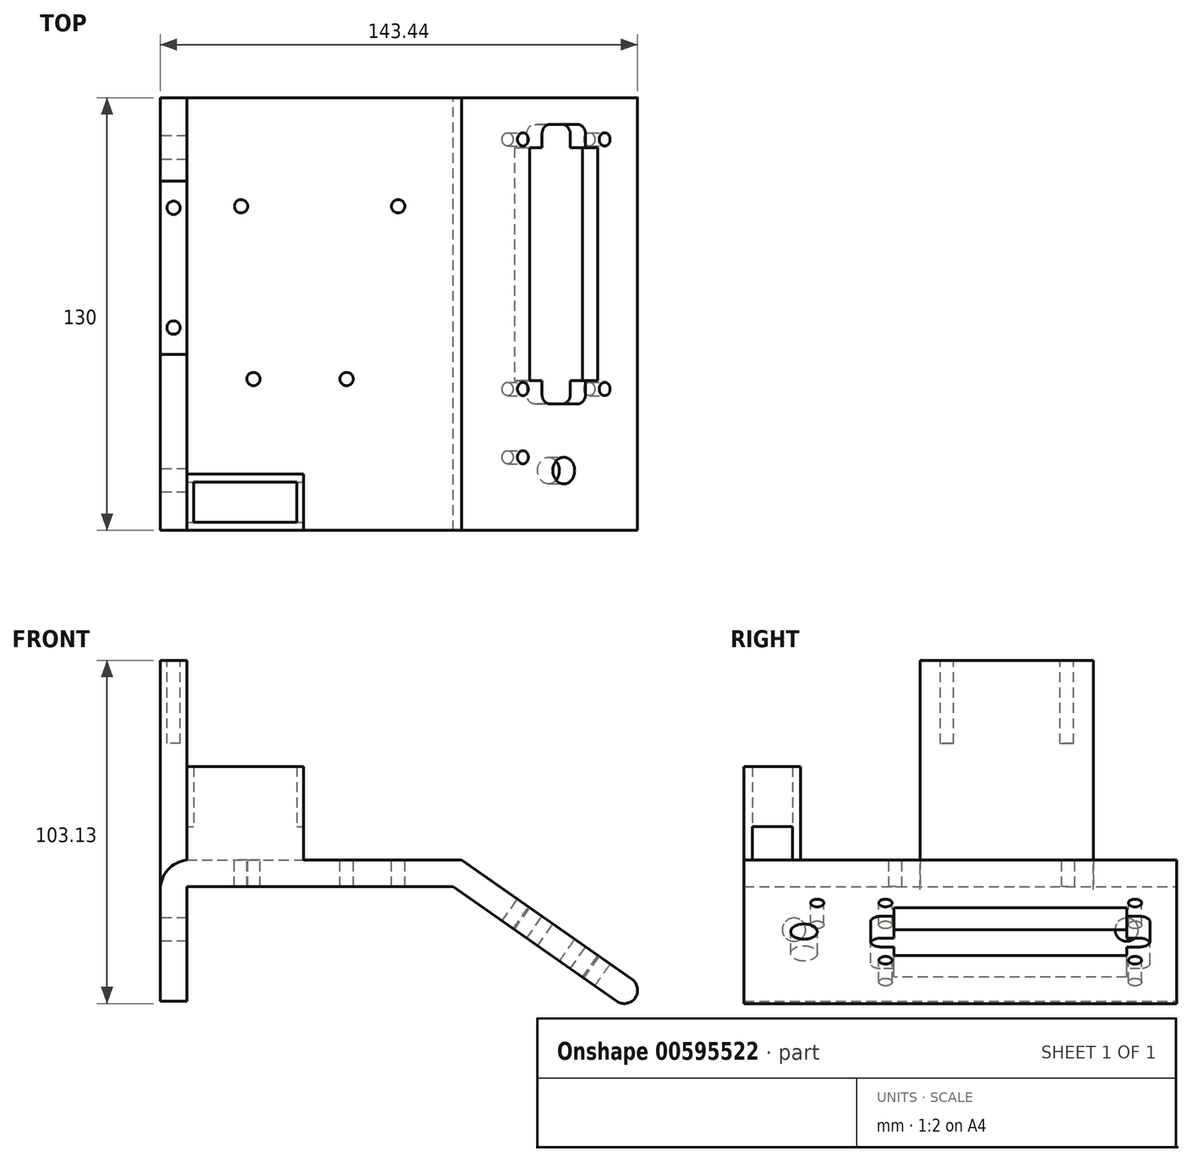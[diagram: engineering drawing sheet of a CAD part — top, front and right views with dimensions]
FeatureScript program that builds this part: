
annotation { "Feature Type Name" : "Feature", "Feature Type Description" : "" }
export const myFeature = defineFeature(function(context is Context, id is Id, definition is map)
    precondition{}
    {
        {
            var Q0;
            Q0=qCreatedBy(makeId("Front.planeOp"),FACE);
            var sketch = newSketch(context, id + "F0", { "sketchPlane" : qUnion([Q0])});
            skLineSegment(sketch, "E0", {"start": v(89.15, 0) * mm, "end": v(40, 34.41) * mm});
            skLineSegment(sketch, "E1", {"start": v(40, 34.41) * mm, "end": v(-40, 34.41) * mm});
            skLineSegment(sketch, "E2", {"start": v(-37.03, 0) * mm, "end": v(89.15, 0) * mm, "construction": true});
            skLineSegment(sketch, "E3", {"start": v(0, 34.41) * mm, "end": v(0, 0) * mm, "construction": true});
            skLineSegment(sketch, "E4.0", {"start": v(42.52, 42.41) * mm, "end": v(-40, 42.41) * mm});
            skLineSegment(sketch, "E4.1", {"start": v(93.74, 6.55) * mm, "end": v(42.52, 42.41) * mm});
            skLineSegment(sketch, "E5", {"start": v(-40, 42.41) * mm, "end": v(-40, 34.41) * mm, "construction": true});
            skLineSegment(sketch, "E6", {"start": v(93.74, 6.55) * mm, "end": v(89.15, 0) * mm, "construction": true});
            skArc(sketch, "E7", {"start": v(89.15, 0) * mm, "mid": v(94.72, 0.98) * mm, "end": v(93.74, 6.55) * mm});
            skLineSegment(sketch, "E8", {"start": v(-40, 34.41) * mm, "end": v(-40, 0) * mm});
            skLineSegment(sketch, "E9.0", {"start": v(-48, 33.47) * mm, "end": v(-48, 0) * mm});
            skArc(sketch, "E10", {"start": v(-40, 42.41) * mm, "mid": v(-45.7, 39.47) * mm, "end": v(-48, 33.47) * mm});
            skLineSegment(sketch, "E11", {"start": v(-40, 0) * mm, "end": v(-48, 0) * mm});
            skSolve(sketch);
        }
        {
            var Q0;
            Q0=makeQuery(id+"F0.imprint","IMPRINT",FACE,{"disambiguationData":[TD([[makeQuery(id+"F0.imprint","IMPRINT",EDGE,{"derivedFrom":sQuery(id+"F0.wireOp",EDGE,"E0")}),-1.0]])]});
            extrude(context, id + "F1", {"entities" : qUnion([Q0]), "depth" : 80 * mm, "offsetDistance" : 25 * mm, "hasSecondDirection" : true, "secondDirectionOppositeDirection" : true, "secondDirectionDepth" : 50 * mm});
        }
        {
            var Q0;
            Q0=makeQuery(id+"F1.opExtrude","SWEPT_FACE",FACE,{"disambiguationData":[OSD([sQuery(id+"F0.wireOp",EDGE,"E4.1")])]});
            var sketch = newSketch(context, id + "F2", { "sketchPlane" : qUnion([Q0])});
            skLineSegment(sketch, "E12.bottom", {"start": v(35.53, -35) * mm, "end": v(40.03, -35) * mm});
            skLineSegment(sketch, "E12.top", {"start": v(35.53, 35) * mm, "end": v(60.53, 35) * mm});
            skLineSegment(sketch, "E12.left", {"start": v(35.53, -35) * mm, "end": v(35.53, 35) * mm});
            skLineSegment(sketch, "E12.right", {"start": v(60.53, -35) * mm, "end": v(60.53, 35) * mm});
            skPoint(sketch, "E12.middle", {"position": v(48.03, 0) * mm});
            skLineSegment(sketch, "E13.bottom", {"start": v(63.03, 37.5) * mm, "end": v(33.03, 37.5) * mm, "construction": true});
            skLineSegment(sketch, "E13.top", {"start": v(63.03, -37.5) * mm, "end": v(33.03, -37.5) * mm, "construction": true});
            skLineSegment(sketch, "E13.left", {"start": v(63.03, 37.5) * mm, "end": v(63.03, -37.5) * mm, "construction": true});
            skLineSegment(sketch, "E13.right", {"start": v(33.03, 37.5) * mm, "end": v(33.03, -37.5) * mm, "construction": true});
            skCircle(sketch, "E14", {"center": v(33.03, -37.5) * mm, "radius": 2 * mm});
            skCircle(sketch, "E15", {"center": v(33.03, 37.5) * mm, "radius": 2 * mm});
            skCircle(sketch, "E16", {"center": v(63.03, 37.5) * mm, "radius": 2 * mm});
            skCircle(sketch, "E17", {"center": v(63.03, -37.5) * mm, "radius": 2 * mm});
            skLineSegment(sketch, "E18.bottom", {"start": v(43.03, -42) * mm, "end": v(53.03, -42) * mm});
            skLineSegment(sketch, "E18.top", {"start": v(40.03, -28) * mm, "end": v(56.03, -28) * mm, "construction": true});
            skLineSegment(sketch, "E18.left", {"start": v(40.03, -39) * mm, "end": v(40.03, -35) * mm});
            skLineSegment(sketch, "E18.right", {"start": v(56.03, -39) * mm, "end": v(56.03, -35) * mm});
            skPoint(sketch, "E18.middle", {"position": v(48.03, -35) * mm});
            skLineSegment(sketch, "E19", {"start": v(40.03, -35) * mm, "end": v(40.03, -28) * mm, "construction": true});
            skLineSegment(sketch, "E20", {"start": v(56.03, -35) * mm, "end": v(56.03, -28) * mm, "construction": true});
            skLineSegment(sketch, "E21", {"start": v(56.03, -35) * mm, "end": v(60.53, -35) * mm});
            skLineSegment(sketch, "E22", {"start": v(40.03, -35) * mm, "end": v(56.03, -35) * mm, "construction": true});
            skLineSegment(sketch, "E23", {"start": v(10.5, -15) * mm, "end": v(73.03, -15) * mm, "construction": true});
            skPoint(sketch, "E24.visualSharp", {"position": v(40.03, -42) * mm});
            skArc(sketch, "E24.filletArc", {"start": v(40.03, -39) * mm, "mid": v(40.9, -41.12) * mm, "end": v(43.03, -42) * mm});
            skPoint(sketch, "E25.visualSharp", {"position": v(56.03, -42) * mm});
            skArc(sketch, "E25.filletArc", {"start": v(53.03, -42) * mm, "mid": v(55.15, -41.12) * mm, "end": v(56.03, -39) * mm});
            skLineSegment(sketch, "E26.bottom", {"start": v(40.03, 28) * mm, "end": v(56.03, 28) * mm, "construction": true});
            skLineSegment(sketch, "E26.top", {"start": v(43.03, 42) * mm, "end": v(53.03, 42) * mm});
            skLineSegment(sketch, "E26.left", {"start": v(40.03, 28) * mm, "end": v(40.03, 35) * mm, "construction": true});
            skLineSegment(sketch, "E26.right", {"start": v(56.03, 28) * mm, "end": v(56.03, 35) * mm, "construction": true});
            skPoint(sketch, "E26.middle", {"position": v(48.03, 35) * mm});
            skLineSegment(sketch, "E27", {"start": v(40.03, 35) * mm, "end": v(40.03, 35.04) * mm});
            skLineSegment(sketch, "E28", {"start": v(56.03, 35) * mm, "end": v(56.03, 35) * mm});
            skLineSegment(sketch, "E29", {"start": v(40.03, 35.04) * mm, "end": v(40.03, 39) * mm});
            skLineSegment(sketch, "E30", {"start": v(56.03, 35) * mm, "end": v(56.03, 39) * mm});
            skPoint(sketch, "E31.visualSharp", {"position": v(40.03, 42) * mm});
            skArc(sketch, "E31.filletArc", {"start": v(43.03, 42) * mm, "mid": v(40.9, 41.12) * mm, "end": v(40.03, 39) * mm});
            skPoint(sketch, "E32.visualSharp", {"position": v(56.03, 42) * mm});
            skArc(sketch, "E32.filletArc", {"start": v(56.03, 39) * mm, "mid": v(55.15, 41.12) * mm, "end": v(53.03, 42) * mm});
            skSolve(sketch);
        }
        {
            var Q0;
            Q0 = qSketchRegion(id + "F2", true);
            extrude(context, id + "F3", {"entities" : qUnion([Q0]), "operationType" : NewBodyOperationType.REMOVE, "oppositeDirection" : true, "depth" : 25 * mm, "offsetDistance" : 25 * mm});
        }
        {
            var Q0;
            Q0=makeQuery(id+"F1.opExtrude","SWEPT_FACE",FACE,{"disambiguationData":[OSD([sQuery(id+"F0.wireOp",EDGE,"E4.0")])]});
            var sketch = newSketch(context, id + "F4", { "sketchPlane" : qUnion([Q0])});
            skLineSegment(sketch, "E33.bottom", {"start": v(27, 33) * mm, "end": v(-27, 33) * mm, "construction": true});
            skLineSegment(sketch, "E33.top", {"start": v(27, -37) * mm, "end": v(-27, -37) * mm, "construction": true});
            skLineSegment(sketch, "E33.left", {"start": v(27, 33) * mm, "end": v(27, -37) * mm, "construction": true});
            skLineSegment(sketch, "E33.right", {"start": v(-27, 33) * mm, "end": v(-27, -37) * mm, "construction": true});
            skPoint(sketch, "E33.middle", {"position": v(0, -2) * mm});
            skLineSegment(sketch, "E34", {"start": v(40, 13) * mm, "end": v(-42.52, 13) * mm, "construction": true});
            skLineSegment(sketch, "E35", {"start": v(0, 78) * mm, "end": v(0, -52) * mm, "construction": true});
            skPoint(sketch, "E35.startSnap0", {"position": v(-1.26, 78) * mm});
            skCircle(sketch, "E36", {"center": v(8, -34.5) * mm, "radius": 2 * mm});
            skCircle(sketch, "E37", {"center": v(-20, -34.5) * mm, "radius": 2 * mm});
            skCircle(sketch, "E38", {"center": v(23.5, 17.4) * mm, "radius": 2 * mm});
            skCircle(sketch, "E39", {"center": v(-23.7, 17.4) * mm, "radius": 2 * mm});
            skSolve(sketch);
        }
        {
            var Q0;
            Q0 = qSketchRegion(id + "F4", true);
            extrude(context, id + "F5", {"entities" : qUnion([Q0]), "operationType" : NewBodyOperationType.REMOVE, "oppositeDirection" : true, "depth" : 25 * mm, "offsetDistance" : 25 * mm});
        }
        {
            var Q0;
            Q0=makeQuery(id+"F1.opExtrude","SWEPT_FACE",FACE,{"disambiguationData":[OSD([sQuery(id+"F0.wireOp",EDGE,"E4.0")])]});
            var sketch = newSketch(context, id + "F6", { "sketchPlane" : qUnion([Q0])});
            skLineSegment(sketch, "E40.bottom", {"start": v(-40, -80) * mm, "end": v(-5, -80) * mm});
            skLineSegment(sketch, "E40.top", {"start": v(-40, -63) * mm, "end": v(-5, -63) * mm});
            skLineSegment(sketch, "E40.left", {"start": v(-40, -80) * mm, "end": v(-40, -63) * mm});
            skLineSegment(sketch, "E40.right", {"start": v(-5, -80) * mm, "end": v(-5, -63) * mm});
            skLineSegment(sketch, "E41.bottom", {"start": v(-38, -77.5) * mm, "end": v(-7, -77.5) * mm});
            skLineSegment(sketch, "E41.top", {"start": v(-38, -65.5) * mm, "end": v(-7, -65.5) * mm});
            skLineSegment(sketch, "E41.left", {"start": v(-38, -77.5) * mm, "end": v(-38, -65.5) * mm});
            skLineSegment(sketch, "E41.right", {"start": v(-7, -77.5) * mm, "end": v(-7, -65.5) * mm});
            skLineSegment(sketch, "E42", {"start": v(-40, -71.5) * mm, "end": v(-5, -71.5) * mm, "construction": true});
            skLineSegment(sketch, "E43", {"start": v(-22.5, -80) * mm, "end": v(-22.5, -63) * mm, "construction": true});
            skLineSegment(sketch, "E44", {"start": v(-38, -71.5) * mm, "end": v(-7, -71.5) * mm, "construction": true});
            skSolve(sketch);
        }
        {
            var Q0;
            Q0 = qSketchRegion(id + "F6", true);
            extrude(context, id + "F7", {"entities" : qUnion([Q0]), "operationType" : NewBodyOperationType.ADD, "depth" : 28 * mm, "offsetDistance" : 25 * mm});
        }
        {
            var Q0;
            Q0=makeQuery(id+"F7.opExtrude","SWEPT_FACE",FACE,{"disambiguationData":[OSD([sQuery(id+"F6.wireOp",EDGE,"E40.right")])]});
            var sketch = newSketch(context, id + "F8", { "sketchPlane" : qUnion([Q0])});
            skLineSegment(sketch, "E45.bottom", {"start": v(-77.5, 42.41) * mm, "end": v(-65.5, 42.41) * mm});
            skLineSegment(sketch, "E45.top", {"start": v(-77.5, 52.41) * mm, "end": v(-65.5, 52.41) * mm});
            skLineSegment(sketch, "E45.left", {"start": v(-77.5, 42.41) * mm, "end": v(-77.5, 52.41) * mm});
            skLineSegment(sketch, "E45.right", {"start": v(-65.5, 42.41) * mm, "end": v(-65.5, 52.41) * mm});
            skPoint(sketch, "E45.middle", {"position": v(-71.5, 47.41) * mm});
            skLineSegment(sketch, "E46.bottom", {"start": v(-71.5, 42.41) * mm, "end": v(-71.5, 42.41) * mm});
            skLineSegment(sketch, "E46.top", {"start": v(-71.5, 98.41) * mm, "end": v(-71.5, 98.41) * mm});
            skLineSegment(sketch, "E46.left", {"start": v(-71.5, 42.41) * mm, "end": v(-71.5, 98.41) * mm});
            skLineSegment(sketch, "E46.right", {"start": v(-71.5, 42.41) * mm, "end": v(-71.5, 98.41) * mm, "construction": true});
            skPoint(sketch, "E46.middle", {"position": v(-71.5, 70.41) * mm});
            skSolve(sketch);
        }
        {
            var Q0;
            Q0 = qSketchRegion(id + "F8", true);
            extrude(context, id + "F9", {"entities" : qUnion([Q0]), "operationType" : NewBodyOperationType.REMOVE, "endBound" : BoundingType.THROUGH_ALL, "oppositeDirection" : true, "depth" : 25 * mm, "offsetDistance" : 25 * mm});
        }
        {
            var Q0;
            Q0=makeQuery(id+"F1.opExtrude","SWEPT_FACE",FACE,{"disambiguationData":[OSD([sQuery(id+"F0.wireOp",EDGE,"E4.1")])]});
            var sketch = newSketch(context, id + "F10", { "sketchPlane" : qUnion([Q0])});
            skCircle(sketch, "E47", {"center": v(48.03, -62) * mm, "radius": 4 * mm});
            skCircle(sketch, "E48", {"center": v(33.03, -58) * mm, "radius": 2 * mm});
            skSolve(sketch);
        }
        {
            var Q0;
            Q0 = qSketchRegion(id + "F10", true);
            extrude(context, id + "F11", {"entities" : qUnion([Q0]), "operationType" : NewBodyOperationType.REMOVE, "oppositeDirection" : true, "depth" : 25 * mm, "offsetDistance" : 25 * mm});
        }
        {
            var Q0;
            Q0=makeQuery(id+"F1.opExtrude","SWEPT_FACE",FACE,{"disambiguationData":[OSD([sQuery(id+"F0.wireOp",EDGE,"E9.0")])]});
            var sketch = newSketch(context, id + "F12", { "sketchPlane" : qUnion([Q0])});
            skCircle(sketch, "E49", {"center": v(-35, 21.47) * mm, "radius": 3.5 * mm});
            skLineSegment(sketch, "E50", {"start": v(15, 33.47) * mm, "end": v(15, 0) * mm, "construction": true});
            skCircle(sketch, "E51.MirrorC", {"center": v(65, 21.47) * mm, "radius": 3.5 * mm});
            skSolve(sketch);
        }
        {
            var Q0;
            Q0 = qSketchRegion(id + "F12", true);
            extrude(context, id + "F13", {"entities" : qUnion([Q0]), "operationType" : NewBodyOperationType.REMOVE, "endBound" : BoundingType.UP_TO_NEXT, "oppositeDirection" : true, "depth" : 25 * mm, "offsetDistance" : 25 * mm});
        }
        {
            var Q0;
            {var subQ0=sQuery(id+"F0.wireOp",EDGE,"E4.0");var subQ1=makeQuery(id+"F1.opExtrude","SWEPT_FACE",FACE,{"disambiguationData":[OSD([subQ0])]});var subQ7=sQuery(id+"F0.wireOp",EDGE,"E4.1");Q0=makeQuery(id+"F9.boolean.opBoolean","MERGE",FACE,{"derivedFrom":[makeQuery(id+"F7.boolean.opBoolean","SPLIT",FACE,{"disambiguationData":[TD([makeQuery(id+"F1.opExtrude","SWEPT_FACE",FACE,{"disambiguationData":[OSD([subQ7])]})])],"derivedFrom":subQ1}),makeQuery(id+"F7.boolean.opBoolean","SPLIT",FACE,{"disambiguationData":[TD([makeQuery(id+"F7.opExtrude","SWEPT_FACE",FACE,{"disambiguationData":[OSD([sQuery(id+"F6.wireOp",EDGE,"E41.bottom")])]})])],"derivedFrom":subQ1}),makeQuery(id+"F9.opExtrude","SWEPT_FACE",FACE,{"disambiguationData":[OSD([sQuery(id+"F8.wireOp",EDGE,"E45.bottom")])]})]});}
            var sketch = newSketch(context, id + "F14", { "sketchPlane" : qUnion([Q0])});
            skLineSegment(sketch, "E52.bottom", {"start": v(-48, 24.95) * mm, "end": v(-40, 24.95) * mm});
            skLineSegment(sketch, "E52.top", {"start": v(-48, -27.05) * mm, "end": v(-40, -27.05) * mm});
            skLineSegment(sketch, "E52.left", {"start": v(-48, 24.95) * mm, "end": v(-48, -27.05) * mm});
            skLineSegment(sketch, "E52.right", {"start": v(-40, 24.95) * mm, "end": v(-40, -27.05) * mm});
            skSolve(sketch);
        }
        {
            var Q0;
            Q0 = qSketchRegion(id + "F14", true);
            extrude(context, id + "F15", {"entities" : qUnion([Q0]), "operationType" : NewBodyOperationType.ADD, "depth" : 60 * mm, "offsetDistance" : 25 * mm, "hasSecondDirection" : true, "secondDirectionOppositeDirection" : true, "secondDirectionDepth" : 25 * mm});
        }
        {
            var Q0;
            Q0=makeQuery(id+"F15.opExtrude","CAP_FACE",FACE,{"disambiguationData":[OSD([sQuery(id+"F14.wireOp",EDGE,"E52.bottom"),sQuery(id+"F14.wireOp",EDGE,"E52.top"),sQuery(id+"F14.wireOp",EDGE,"E52.left"),sQuery(id+"F14.wireOp",EDGE,"E52.right")])],"isStart":false});
            var sketch = newSketch(context, id + "F16", { "sketchPlane" : qUnion([Q0])});
            skCircle(sketch, "E53", {"center": v(-44, -19.05) * mm, "radius": 2 * mm});
            skLineSegment(sketch, "E54", {"start": v(-44, -27.05) * mm, "end": v(-44, 24.95) * mm, "construction": true});
            skLineSegment(sketch, "E55", {"start": v(-48, -1.05) * mm, "end": v(-40, -1.05) * mm, "construction": true});
            skCircle(sketch, "E56.MirrorC", {"center": v(-44, 16.95) * mm, "radius": 2 * mm});
            skSolve(sketch);
        }
        {
            var Q0;
            Q0 = qSketchRegion(id + "F16", true);
            extrude(context, id + "F17", {"entities" : qUnion([Q0]), "operationType" : NewBodyOperationType.REMOVE, "oppositeDirection" : true, "depth" : 25 * mm, "offsetDistance" : 25 * mm});
        }
    });
